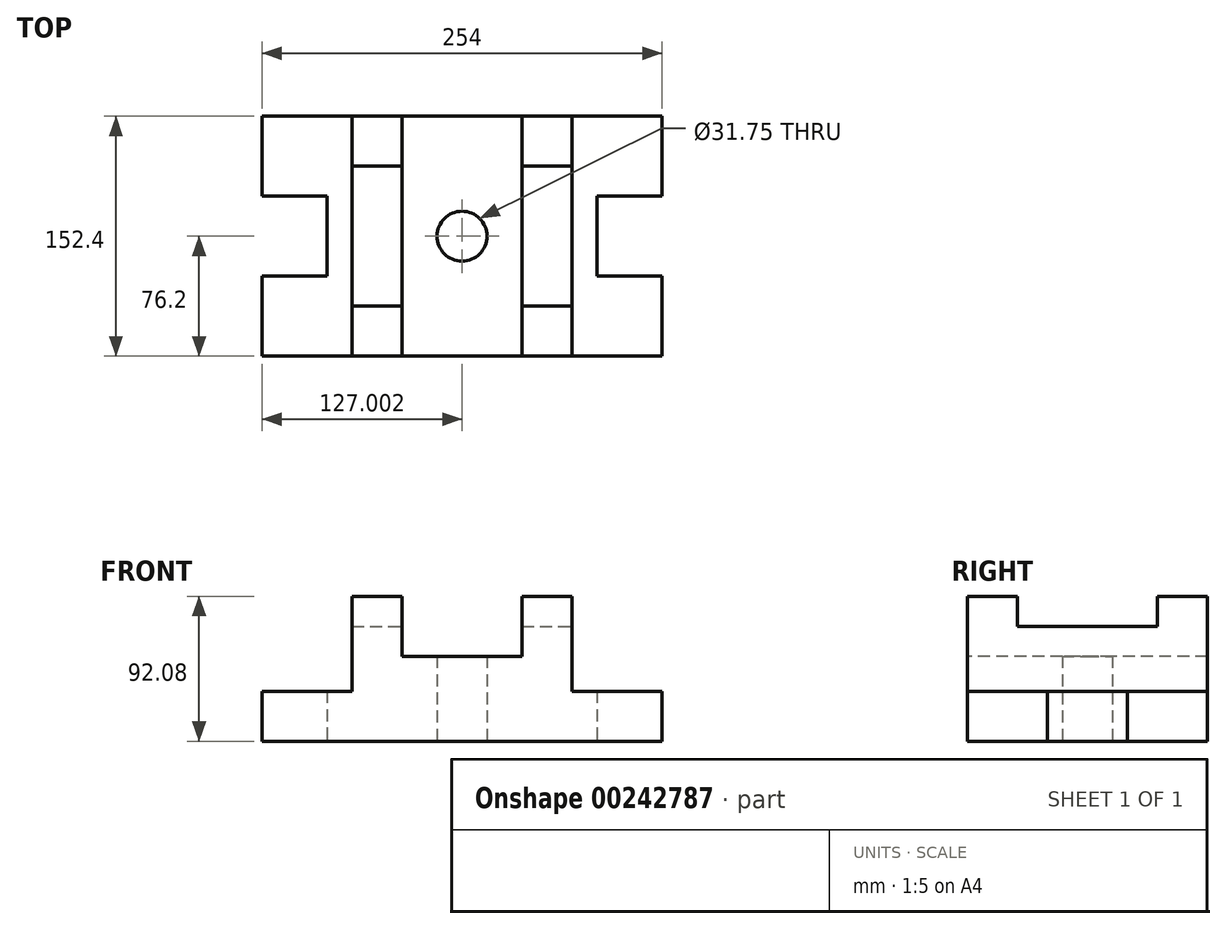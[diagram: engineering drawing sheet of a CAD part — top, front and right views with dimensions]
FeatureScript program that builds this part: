
annotation { "Feature Type Name" : "Feature", "Feature Type Description" : "" }
export const myFeature = defineFeature(function(context is Context, id is Id, definition is map)
    precondition{}
    {
        {
            var Q0;
            Q0=qCreatedBy(makeId("Top.planeOp"),FACE);
            var sketch = newSketch(context, id + "F0", { "sketchPlane" : qUnion([Q0])});
            skLineSegment(sketch, "E0.bottom", {"start": v(-111.2, 50.8) * mm, "end": v(142.8, 50.8) * mm});
            skLineSegment(sketch, "E0.top", {"start": v(-111.2, 0) * mm, "end": v(-69.92, 0) * mm});
            skLineSegment(sketch, "E0.left", {"start": v(-111.2, 50.8) * mm, "end": v(-111.2, 0) * mm});
            skLineSegment(sketch, "E0.right", {"start": v(142.8, 50.8) * mm, "end": v(142.8, 0) * mm});
            skLineSegment(sketch, "E1.bottom", {"start": v(-111.2, -50.8) * mm, "end": v(-69.92, -50.8) * mm});
            skLineSegment(sketch, "E1.top", {"start": v(-111.2, -101.6) * mm, "end": v(142.8, -101.6) * mm});
            skLineSegment(sketch, "E1.left", {"start": v(-111.2, -50.8) * mm, "end": v(-111.2, -101.6) * mm});
            skLineSegment(sketch, "E1.right", {"start": v(142.8, -50.8) * mm, "end": v(142.8, -101.6) * mm});
            skLineSegment(sketch, "E2.left", {"start": v(-69.92, 0) * mm, "end": v(-69.92, -50.8) * mm});
            skLineSegment(sketch, "E2.right", {"start": v(101.53, 0) * mm, "end": v(101.53, -50.8) * mm});
            skLineSegment(sketch, "E3.trimOffspring", {"start": v(101.53, 0) * mm, "end": v(142.8, 0) * mm});
            skLineSegment(sketch, "E4.trimOffspring", {"start": v(101.53, -50.8) * mm, "end": v(142.8, -50.8) * mm});
            skCircle(sketch, "E5", {"center": v(15.8, -25.4) * mm, "radius": 15.88 * mm});
            skSolve(sketch);
        }
        {
            var Q0;
            Q0 = qSketchRegion(id + "F0", true);
            extrude(context, id + "F1", {"entities" : qUnion([Q0]), "depth" : 31.75 * mm});
        }
        {
            var Q0;
            Q0=makeQuery(id+"F1.opExtrude","CAP_FACE",FACE,{"disambiguationData":[OSD([sQuery(id+"F0.wireOp",EDGE,"E0.bottom"),sQuery(id+"F0.wireOp",EDGE,"E0.top"),sQuery(id+"F0.wireOp",EDGE,"E0.left"),sQuery(id+"F0.wireOp",EDGE,"E0.right"),sQuery(id+"F0.wireOp",EDGE,"E1.bottom"),sQuery(id+"F0.wireOp",EDGE,"E1.top"),sQuery(id+"F0.wireOp",EDGE,"E1.left"),sQuery(id+"F0.wireOp",EDGE,"E1.right"),sQuery(id+"F0.wireOp",EDGE,"E2.left"),sQuery(id+"F0.wireOp",EDGE,"E2.right"),sQuery(id+"F0.wireOp",EDGE,"E3.trimOffspring"),sQuery(id+"F0.wireOp",EDGE,"E4.trimOffspring")])],"isStart":false});
            var sketch = newSketch(context, id + "F2", { "sketchPlane" : qUnion([Q0])});
            skLineSegment(sketch, "E6.bottom", {"start": v(-54.05, 50.8) * mm, "end": v(85.65, 50.8) * mm});
            skLineSegment(sketch, "E6.top", {"start": v(-54.05, -101.6) * mm, "end": v(85.65, -101.6) * mm});
            skLineSegment(sketch, "E6.left", {"start": v(-54.05, 50.8) * mm, "end": v(-54.05, -101.6) * mm});
            skLineSegment(sketch, "E6.right", {"start": v(85.65, 50.8) * mm, "end": v(85.65, -101.6) * mm});
            skCircle(sketch, "E7", {"center": v(15.8, -25.4) * mm, "radius": 15.88 * mm});
            skSolve(sketch);
        }
        {
            var Q0;
            Q0=makeQuery(id+"F2.imprint","IMPRINT",FACE,{"disambiguationData":[TD([[makeQuery(id+"F2.imprint","IMPRINT",EDGE,{"derivedFrom":sQuery(id+"F2.wireOp",EDGE,"E6.bottom")}),-1.0]])]});
            extrude(context, id + "F3", {"entities" : qUnion([Q0]), "operationType" : NewBodyOperationType.ADD, "depth" : 22.22 * mm});
        }
        {
            var Q0;
            Q0=makeQuery(id+"F3.opExtrude","CAP_FACE",FACE,{"disambiguationData":[OSD([sQuery(id+"F2.wireOp",EDGE,"E6.bottom"),sQuery(id+"F2.wireOp",EDGE,"E6.top"),sQuery(id+"F2.wireOp",EDGE,"E6.left"),sQuery(id+"F2.wireOp",EDGE,"E6.right"),sQuery(id+"F2.wireOp",EDGE,"E7")])],"isStart":false});
            var sketch = newSketch(context, id + "F4", { "sketchPlane" : qUnion([Q0])});
            skLineSegment(sketch, "E8.bottom", {"start": v(-54.05, 50.8) * mm, "end": v(-22.3, 50.8) * mm});
            skLineSegment(sketch, "E8.top", {"start": v(-54.05, -101.6) * mm, "end": v(-22.3, -101.6) * mm});
            skLineSegment(sketch, "E8.left", {"start": v(-54.05, 50.8) * mm, "end": v(-54.05, -101.6) * mm});
            skLineSegment(sketch, "E8.right", {"start": v(-22.3, 50.8) * mm, "end": v(-22.3, -101.6) * mm});
            skLineSegment(sketch, "E9.bottom", {"start": v(85.65, 50.8) * mm, "end": v(53.9, 50.8) * mm});
            skLineSegment(sketch, "E9.top", {"start": v(85.65, -101.6) * mm, "end": v(53.9, -101.6) * mm});
            skLineSegment(sketch, "E9.left", {"start": v(85.65, 50.8) * mm, "end": v(85.65, -101.6) * mm});
            skLineSegment(sketch, "E9.right", {"start": v(53.9, 50.8) * mm, "end": v(53.9, -101.6) * mm});
            skSolve(sketch);
        }
        {
            var Q0;
            Q0=makeQuery(id+"F4.imprint","IMPRINT",FACE,{"disambiguationData":[TD([[makeQuery(id+"F4.imprint","IMPRINT",EDGE,{"derivedFrom":sQuery(id+"F4.wireOp",EDGE,"E9.bottom")}),-1.0]])]});
            var Q1;
            Q1=makeQuery(id+"F4.imprint","IMPRINT",FACE,{"disambiguationData":[TD([[makeQuery(id+"F4.imprint","IMPRINT",EDGE,{"derivedFrom":sQuery(id+"F4.wireOp",EDGE,"E8.bottom")}),-1.0]])]});
            extrude(context, id + "F5", {"entities" : qUnion([Q0, Q1]), "operationType" : NewBodyOperationType.ADD, "depth" : 19.05 * mm});
        }
        {
            var Q0;
            Q0=makeQuery(id+"F5.opExtrude","CAP_FACE",FACE,{"disambiguationData":[OSD([sQuery(id+"F4.wireOp",EDGE,"E8.bottom"),sQuery(id+"F4.wireOp",EDGE,"E8.top"),sQuery(id+"F4.wireOp",EDGE,"E8.left"),sQuery(id+"F4.wireOp",EDGE,"E8.right")])],"isStart":false});
            var sketch = newSketch(context, id + "F6", { "sketchPlane" : qUnion([Q0])});
            skLineSegment(sketch, "E10.bottom", {"start": v(-54.05, 50.8) * mm, "end": v(-22.3, 50.8) * mm});
            skLineSegment(sketch, "E10.top", {"start": v(-54.05, 19.05) * mm, "end": v(-22.3, 19.05) * mm});
            skLineSegment(sketch, "E10.left", {"start": v(-54.05, 50.8) * mm, "end": v(-54.05, 19.05) * mm});
            skLineSegment(sketch, "E10.right", {"start": v(-22.3, 50.8) * mm, "end": v(-22.3, 19.05) * mm});
            skLineSegment(sketch, "E11.bottom", {"start": v(-54.05, -101.6) * mm, "end": v(-22.3, -101.6) * mm});
            skLineSegment(sketch, "E11.top", {"start": v(-54.05, -69.85) * mm, "end": v(-22.3, -69.85) * mm});
            skLineSegment(sketch, "E11.left", {"start": v(-54.05, -101.6) * mm, "end": v(-54.05, -69.85) * mm});
            skLineSegment(sketch, "E11.right", {"start": v(-22.3, -101.6) * mm, "end": v(-22.3, -69.85) * mm});
            skSolve(sketch);
        }
        {
            var Q0;
            Q0=makeQuery(id+"F6.imprint","IMPRINT",FACE,{"disambiguationData":[TD([[makeQuery(id+"F6.imprint","IMPRINT",EDGE,{"derivedFrom":sQuery(id+"F6.wireOp",EDGE,"E10.bottom")}),-1.0]])]});
            var Q1;
            Q1=makeQuery(id+"F6.imprint","IMPRINT",FACE,{"disambiguationData":[TD([[makeQuery(id+"F6.imprint","IMPRINT",EDGE,{"derivedFrom":sQuery(id+"F6.wireOp",EDGE,"E11.bottom")}),1.0]])]});
            extrude(context, id + "F7", {"entities" : qUnion([Q0, Q1]), "operationType" : NewBodyOperationType.ADD, "depth" : 19.05 * mm});
        }
        {
            var Q0;
            Q0=makeQuery(id+"F5.opExtrude","CAP_FACE",FACE,{"disambiguationData":[OSD([sQuery(id+"F4.wireOp",EDGE,"E9.bottom"),sQuery(id+"F4.wireOp",EDGE,"E9.top"),sQuery(id+"F4.wireOp",EDGE,"E9.left"),sQuery(id+"F4.wireOp",EDGE,"E9.right")])],"isStart":false});
            var sketch = newSketch(context, id + "F8", { "sketchPlane" : qUnion([Q0])});
            skLineSegment(sketch, "E12.bottom", {"start": v(53.9, 50.8) * mm, "end": v(85.65, 50.8) * mm});
            skLineSegment(sketch, "E12.top", {"start": v(53.9, 19.05) * mm, "end": v(85.65, 19.05) * mm});
            skLineSegment(sketch, "E12.left", {"start": v(53.9, 50.8) * mm, "end": v(53.9, 19.05) * mm});
            skLineSegment(sketch, "E12.right", {"start": v(85.65, 50.8) * mm, "end": v(85.65, 19.05) * mm});
            skLineSegment(sketch, "E13.bottom", {"start": v(53.9, -101.6) * mm, "end": v(85.65, -101.6) * mm});
            skLineSegment(sketch, "E13.top", {"start": v(53.9, -69.85) * mm, "end": v(85.65, -69.85) * mm});
            skLineSegment(sketch, "E13.left", {"start": v(53.9, -101.6) * mm, "end": v(53.9, -69.85) * mm});
            skLineSegment(sketch, "E13.right", {"start": v(85.65, -101.6) * mm, "end": v(85.65, -69.85) * mm});
            skSolve(sketch);
        }
        {
            var Q0;
            Q0=makeQuery(id+"F8.imprint","IMPRINT",FACE,{"disambiguationData":[TD([[makeQuery(id+"F8.imprint","IMPRINT",EDGE,{"derivedFrom":sQuery(id+"F8.wireOp",EDGE,"E12.bottom")}),-1.0]])]});
            var Q1;
            Q1=makeQuery(id+"F8.imprint","IMPRINT",FACE,{"disambiguationData":[TD([[makeQuery(id+"F8.imprint","IMPRINT",EDGE,{"derivedFrom":sQuery(id+"F8.wireOp",EDGE,"E13.bottom")}),1.0]])]});
            extrude(context, id + "F9", {"entities" : qUnion([Q0, Q1]), "operationType" : NewBodyOperationType.ADD, "depth" : 19.05 * mm});
        }
    });
